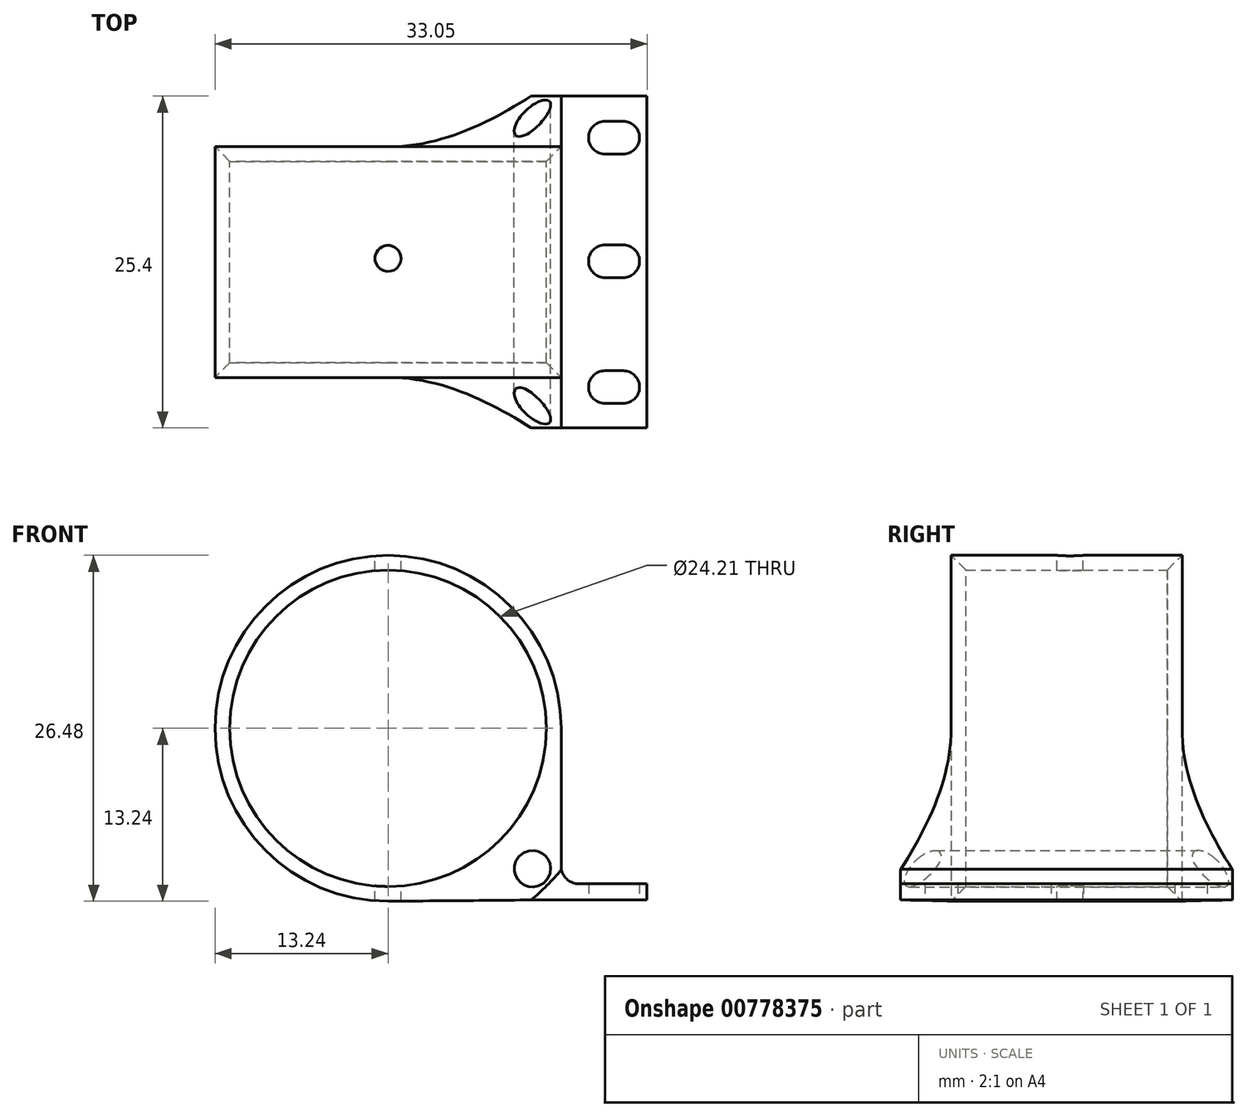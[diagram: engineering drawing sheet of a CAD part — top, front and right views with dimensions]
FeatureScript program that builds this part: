
annotation { "Feature Type Name" : "Feature", "Feature Type Description" : "" }
export const myFeature = defineFeature(function(context is Context, id is Id, definition is map)
    precondition{}
    {
        {
            var Q0;
            Q0=qCreatedBy(makeId("Front.planeOp"),FACE);
            var sketch = newSketch(context, id + "F0", { "sketchPlane" : qUnion([Q0])});
            skCircle(sketch, "E0", {"center": v(0, 0) * mm, "radius": 12.1 * mm});
            skCircle(sketch, "E1", {"center": v(0, 0) * mm, "radius": 13.24 * mm});
            skLineSegment(sketch, "E2", {"start": v(13.24, 0) * mm, "end": v(13.24, -13.12) * mm});
            skLineSegment(sketch, "E3", {"start": v(13.24, -13.12) * mm, "end": v(0, -13.24) * mm});
            skCircle(sketch, "E4", {"center": v(11.04, -10.74) * mm, "radius": 1.4 * mm});
            skLineSegment(sketch, "E5", {"start": v(13.24, -13.12) * mm, "end": v(19.8, -13.12) * mm});
            skLineSegment(sketch, "E6", {"start": v(19.8, -13.12) * mm, "end": v(19.8, -11.9) * mm});
            skLineSegment(sketch, "E7", {"start": v(19.8, -11.9) * mm, "end": v(14.61, -11.9) * mm});
            skArc(sketch, "E8", {"start": v(13.24, -10.77) * mm, "mid": v(13.72, -11.58) * mm, "end": v(14.61, -11.9) * mm});
            skSolve(sketch);
        }
        {
            var Q0;
            Q0 = qSketchRegion(id + "F0", true);
            extrude(context, id + "F1", {"entities" : qUnion([Q0]), "depth" : 25.4 * mm, "offsetDistance" : 25.4 * mm});
        }
        {
            var Q0;
            Q0=qCreatedBy(makeId("Top.planeOp"),FACE);
            cPlane(context, id + "F2", {"entities" : qUnion([Q0]), "cplaneType" : CPlaneType.OFFSET, "offset" : 13.2 * mm, "oppositeDirection" : true, "width" : 152.4 * mm, "height" : 152.4 * mm});
        }
        {
            var Q0;
            Q0=qCreatedBy(id+"F2.planeOp",FACE);
            var sketch = newSketch(context, id + "F3", { "sketchPlane" : qUnion([Q0])});
            skPoint(sketch, "E9.startSnap0", {"position": v(17.99, -12.64) * mm});
            skLineSegment(sketch, "E10", {"start": v(14.75, -3.18) * mm, "end": v(15.34, -3.18) * mm, "construction": true});
            skLineSegment(sketch, "E11", {"start": v(19.84, 0) * mm, "end": v(17.99, 0) * mm, "construction": true});
            skArc(sketch, "E12", {"start": v(17.99, -4.43) * mm, "mid": v(19.24, -3.18) * mm, "end": v(17.99, -1.93) * mm});
            skPoint(sketch, "E12.centerSnap0", {"position": v(17.3, -3.18) * mm});
            skArc(sketch, "E13", {"start": v(17.99, -13.9) * mm, "mid": v(19.24, -12.64) * mm, "end": v(17.99, -11.4) * mm});
            skArc(sketch, "E14", {"start": v(17.99, -23.52) * mm, "mid": v(19.24, -22.27) * mm, "end": v(17.99, -21.02) * mm});
            skLineSegment(sketch, "E15", {"start": v(17.99, -11.4) * mm, "end": v(16.59, -11.4) * mm});
            skLineSegment(sketch, "E16", {"start": v(17.99, -13.9) * mm, "end": v(16.59, -13.9) * mm});
            skArc(sketch, "E17", {"start": v(16.59, -11.4) * mm, "mid": v(15.34, -12.64) * mm, "end": v(16.59, -13.9) * mm});
            skLineSegment(sketch, "E18", {"start": v(17.99, -1.93) * mm, "end": v(16.59, -1.93) * mm});
            skLineSegment(sketch, "E19", {"start": v(17.99, -4.43) * mm, "end": v(16.59, -4.43) * mm});
            skArc(sketch, "E20", {"start": v(16.59, -1.93) * mm, "mid": v(15.34, -3.18) * mm, "end": v(16.59, -4.43) * mm});
            skLineSegment(sketch, "E21", {"start": v(17.99, -21.02) * mm, "end": v(16.59, -21.02) * mm});
            skLineSegment(sketch, "E22", {"start": v(17.99, -23.52) * mm, "end": v(16.59, -23.52) * mm});
            skArc(sketch, "E23", {"start": v(16.59, -21.02) * mm, "mid": v(15.34, -22.27) * mm, "end": v(16.59, -23.52) * mm});
            skPoint(sketch, "E9.start.orphan", {"position": v(19.84, -12.64) * mm});
            skPoint(sketch, "E24.orphan", {"position": v(16.59, 0) * mm});
            skPoint(sketch, "E25.trimOffspring.end.orphan", {"position": v(19.84, -3.18) * mm});
            skPoint(sketch, "E26.trimOffspring.end.orphan", {"position": v(17.99, -25.28) * mm});
            skSolve(sketch);
        }
        {
            var Q0;
            Q0 = qSketchRegion(id + "F3", true);
            extrude(context, id + "F4", {"entities" : qUnion([Q0]), "operationType" : NewBodyOperationType.REMOVE, "depth" : 1.7 * mm, "offsetDistance" : 25 * mm});
        }
        {
            var Q0;
            Q0=makeQuery(id+"F1.opExtrude","CAP_EDGE",EDGE,{"disambiguationData":[OSD([sQuery(id+"F0.wireOp",EDGE,"E0")])],"isStart":false});
            chamfer(context, id + "F5", {"entities" : qUnion([Q0]), "width" : 5 * mm, "tangentPropagation" : true});
        }
        {
            var Q0;
            Q0=makeQuery(id+"F1.opExtrude","CAP_EDGE",EDGE,{"disambiguationData":[OSD([sQuery(id+"F0.wireOp",EDGE,"E0")])],"isStart":true});
            chamfer(context, id + "F6", {"entities" : qUnion([Q0]), "width" : 5 * mm, "tangentPropagation" : true});
        }
        {
            var Q0;
            Q0=qCreatedBy(id+"F2.planeOp",FACE);
            cPlane(context, id + "F7", {"entities" : qUnion([Q0]), "cplaneType" : CPlaneType.OFFSET, "offset" : 26.7 * mm, "width" : 150 * mm, "height" : 150 * mm});
        }
        {
            var Q0;
            Q0=qCreatedBy(id+"F7.planeOp",FACE);
            var sketch = newSketch(context, id + "F8", { "sketchPlane" : qUnion([Q0])});
            skCircle(sketch, "E27", {"center": v(0, -12.42) * mm, "radius": 1 * mm});
            skSolve(sketch);
        }
        {
            var Q0;
            Q0 = qSketchRegion(id + "F8", true);
            extrude(context, id + "F9", {"entities" : qUnion([Q0]), "operationType" : NewBodyOperationType.REMOVE, "oppositeDirection" : true, "depth" : 27.8 * mm, "offsetDistance" : 25 * mm});
        }
    });
